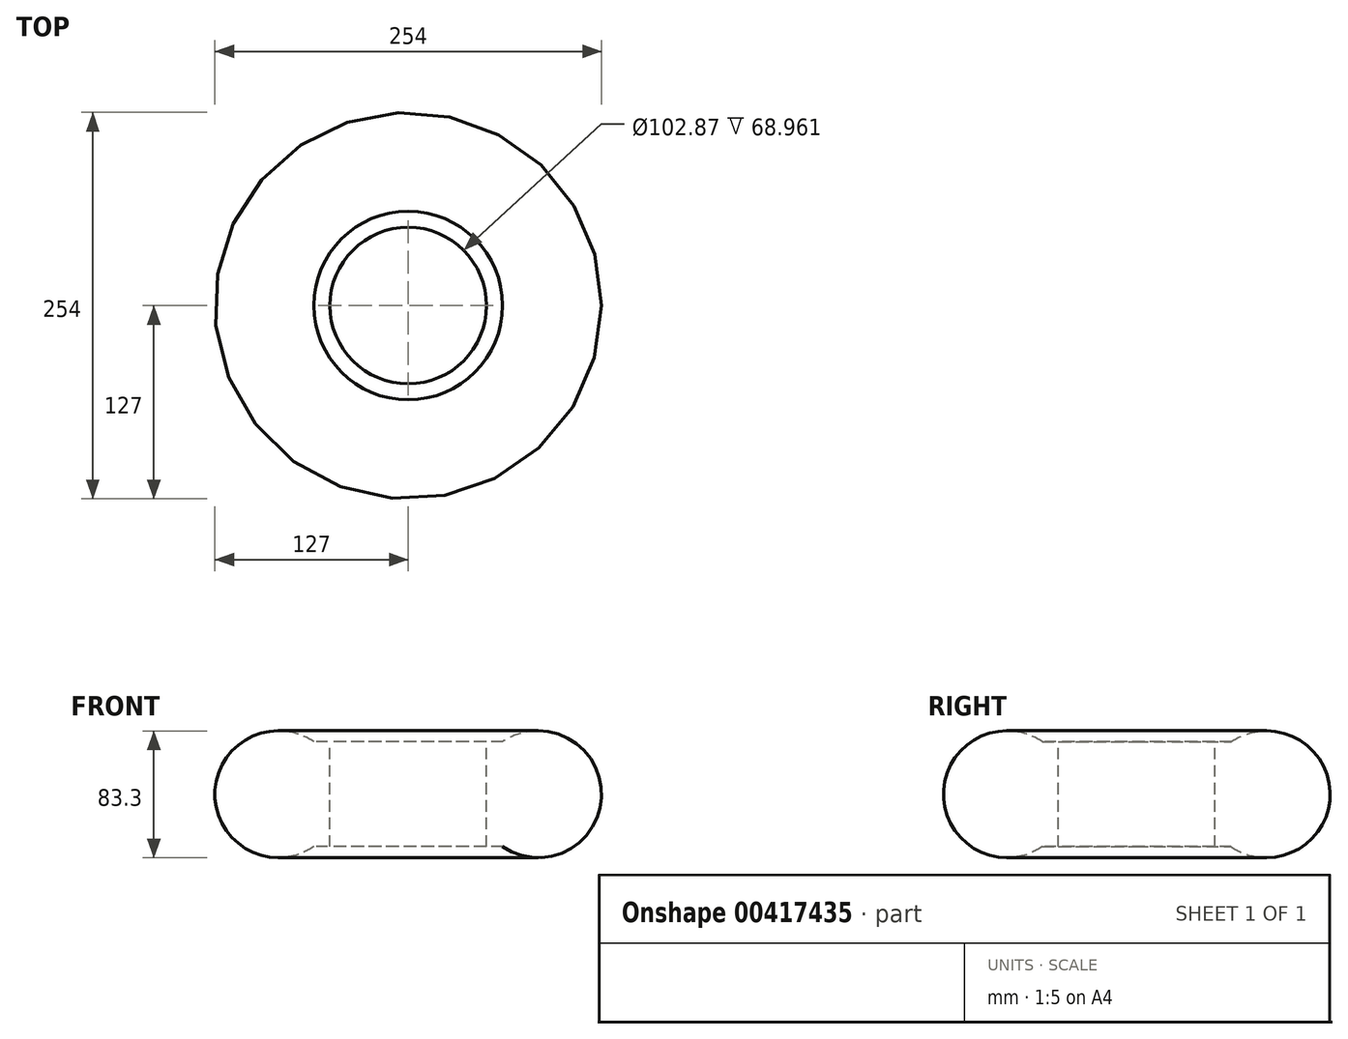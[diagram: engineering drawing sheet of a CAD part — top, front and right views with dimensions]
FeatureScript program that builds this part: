
annotation { "Feature Type Name" : "Feature", "Feature Type Description" : "" }
export const myFeature = defineFeature(function(context is Context, id is Id, definition is map)
    precondition{}
    {
        {
            var Q0;
            Q0=qCreatedBy(makeId("Front.planeOp"),FACE);
            var sketch = newSketch(context, id + "F0", { "sketchPlane" : qUnion([Q0])});
            skLineSegment(sketch, "E0", {"start": v(0, 111.47) * mm, "end": v(0, -106.6) * mm, "construction": true});
            skLineSegment(sketch, "E1", {"start": v(51.44, 34.48) * mm, "end": v(51.44, -34.48) * mm});
            skPoint(sketch, "E2", {"position": v(51.44, 0) * mm});
            skLineSegment(sketch, "E3", {"start": v(51.44, 34.48) * mm, "end": v(61.98, 34.48) * mm});
            skLineSegment(sketch, "E4", {"start": v(51.44, -34.48) * mm, "end": v(61.98, -34.48) * mm});
            skArc(sketch, "E5", {"start": v(61.98, -34.48) * mm, "mid": v(127, 0) * mm, "end": v(61.98, 34.48) * mm});
            skPoint(sketch, "E6", {"position": v(127, 0) * mm});
            skSolve(sketch);
        }
        {
            var Q0;
            Q0=makeQuery(id+"F0.imprint","IMPRINT",FACE,{"disambiguationData":[TD([[makeQuery(id+"F0.imprint","IMPRINT",EDGE,{"derivedFrom":sQuery(id+"F0.wireOp",EDGE,"E1")}),1.0]])]});
            var Q1;
            Q1=sQuery(id+"F0.wireOp",EDGE,"E0");
            revolve(context, id + "F1", {"entities" : qUnion([Q0]), "axis" : qUnion([Q1]), "revolveType" : RevolveType.FULL});
        }
    });
